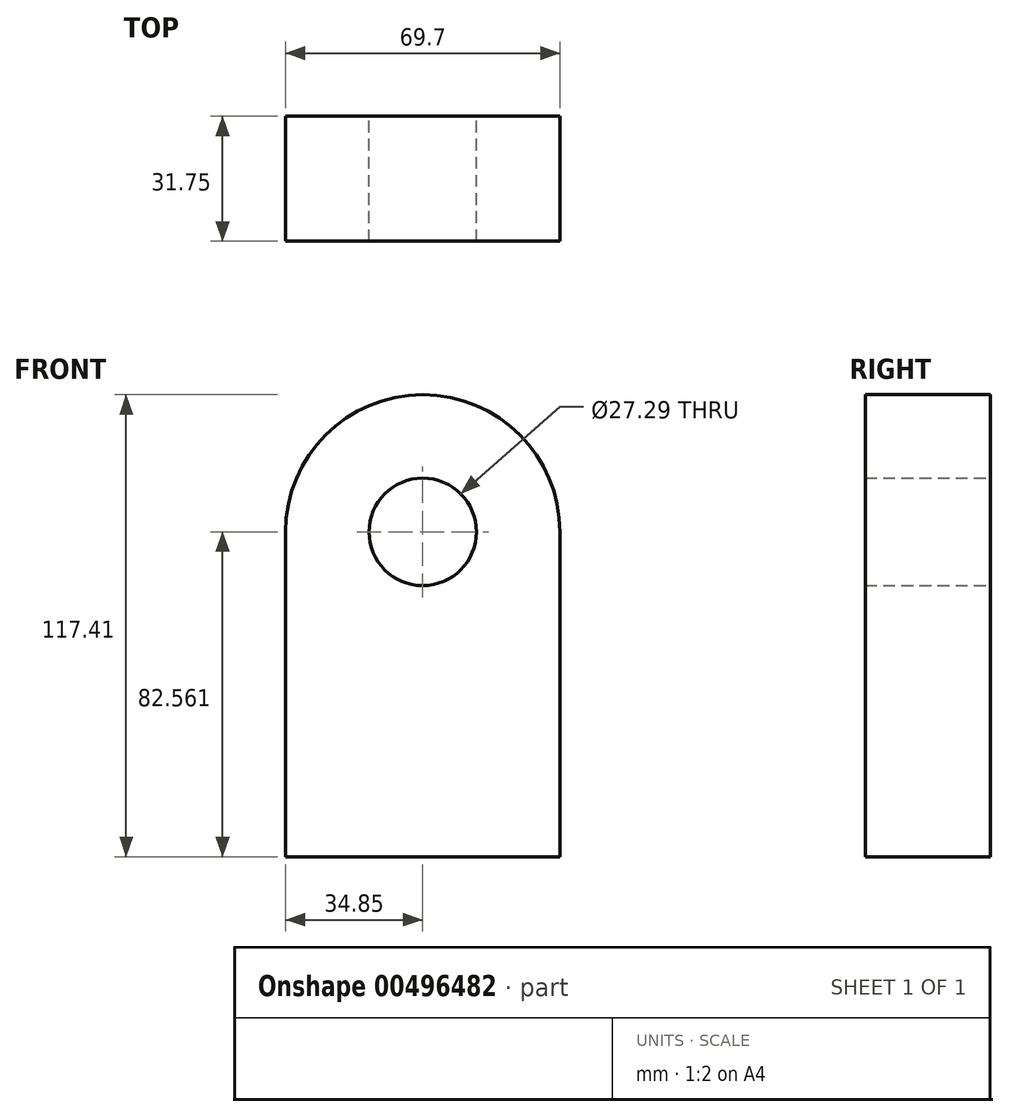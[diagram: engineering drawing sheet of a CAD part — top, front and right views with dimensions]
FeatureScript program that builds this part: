
annotation { "Feature Type Name" : "Feature", "Feature Type Description" : "" }
export const myFeature = defineFeature(function(context is Context, id is Id, definition is map)
    precondition{}
    {
        {
            var Q0;
            Q0=qCreatedBy(makeId("Front.planeOp"),FACE);
            var sketch = newSketch(context, id + "F0", { "sketchPlane" : qUnion([Q0])});
            skLineSegment(sketch, "E0.top", {"start": v(34.85, -41.28) * mm, "end": v(-34.85, -41.28) * mm});
            skLineSegment(sketch, "E0.left", {"start": v(34.85, 41.28) * mm, "end": v(34.85, -41.28) * mm});
            skLineSegment(sketch, "E0.right", {"start": v(-34.85, 41.28) * mm, "end": v(-34.85, -41.28) * mm});
            skPoint(sketch, "E0.middle", {"position": v(0, 0) * mm});
            skArc(sketch, "E1", {"start": v(34.85, 41.28) * mm, "mid": v(0, 76.13) * mm, "end": v(-34.85, 41.28) * mm});
            skCircle(sketch, "E2", {"center": v(0, 41.28) * mm, "radius": 13.65 * mm});
            skSolve(sketch);
        }
        {
            var Q0;
            Q0=makeQuery(id+"F0.imprint","IMPRINT",FACE,{"disambiguationData":[TD([[makeQuery(id+"F0.imprint","IMPRINT",EDGE,{"derivedFrom":sQuery(id+"F0.wireOp",EDGE,"E0.top")}),-1.0]])]});
            extrude(context, id + "F1", {"entities" : qUnion([Q0]), "depth" : 31.75 * mm});
        }
    });
